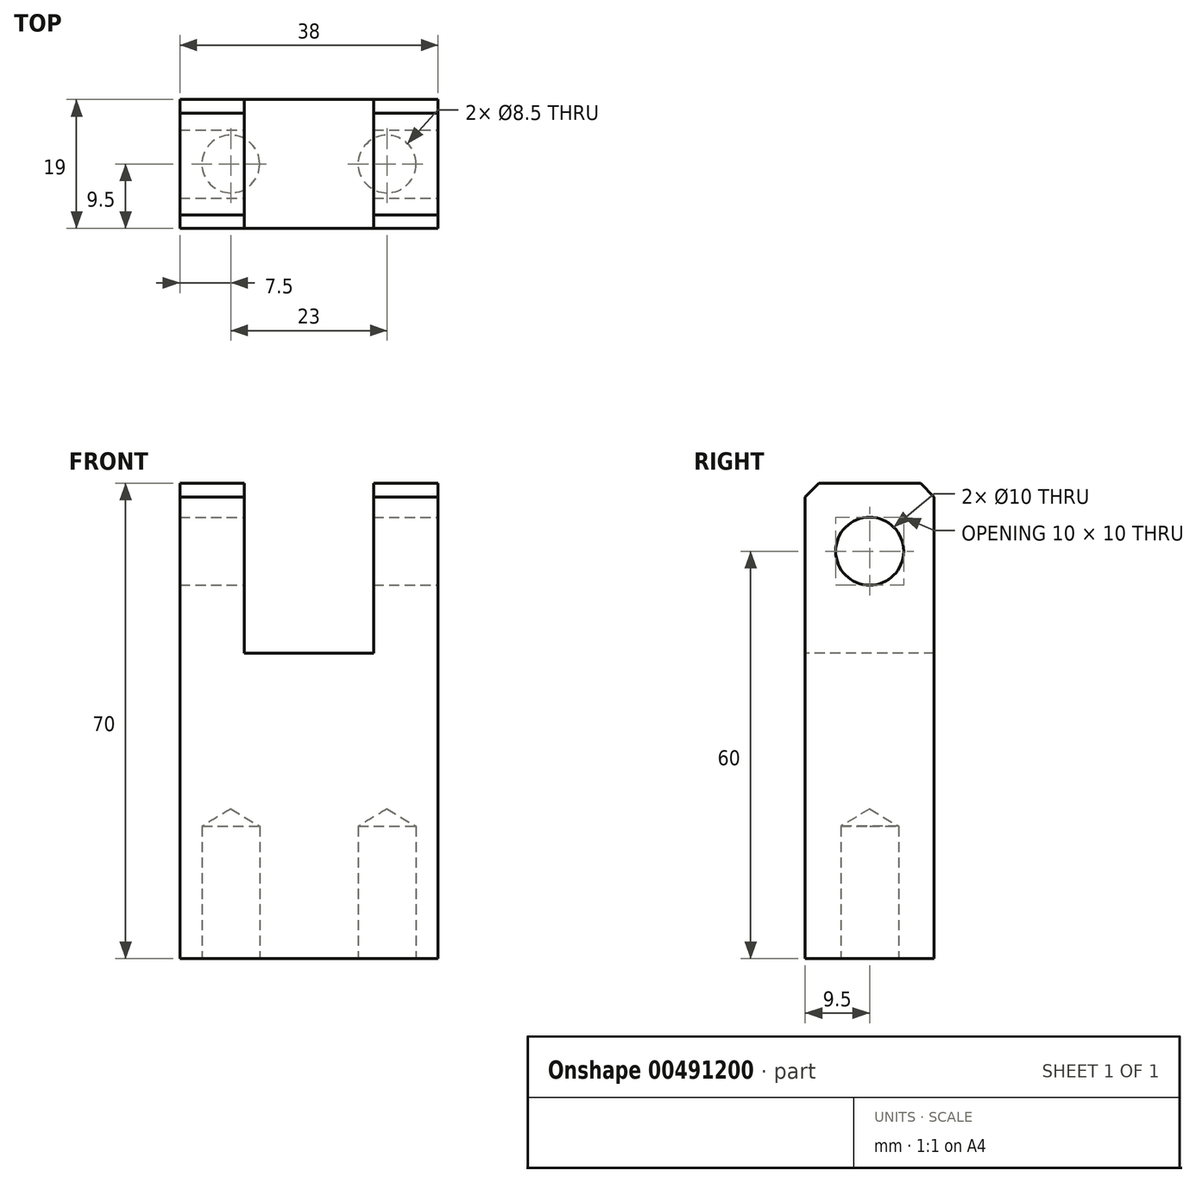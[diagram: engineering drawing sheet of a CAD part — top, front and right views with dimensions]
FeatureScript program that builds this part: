
annotation { "Feature Type Name" : "Feature", "Feature Type Description" : "" }
export const myFeature = defineFeature(function(context is Context, id is Id, definition is map)
    precondition{}
    {
        {
            var Q0;
            Q0=qCreatedBy(makeId("Front.planeOp"),FACE);
            var sketch = newSketch(context, id + "F0", { "sketchPlane" : qUnion([Q0])});
            skLineSegment(sketch, "E0.bottom", {"start": v(-19, 35) * mm, "end": v(19, 35) * mm});
            skLineSegment(sketch, "E0.top", {"start": v(-19, -35) * mm, "end": v(19, -35) * mm});
            skLineSegment(sketch, "E0.left", {"start": v(-19, 35) * mm, "end": v(-19, -35) * mm});
            skLineSegment(sketch, "E0.right", {"start": v(19, 35) * mm, "end": v(19, -35) * mm});
            skSolve(sketch);
        }
        {
            var Q0;
            Q0=makeQuery(id+"F0.imprint","IMPRINT",FACE,{"disambiguationData":[TD([[makeQuery(id+"F0.imprint","IMPRINT",EDGE,{"derivedFrom":sQuery(id+"F0.wireOp",EDGE,"E0.bottom")}),-1.0]])]});
            extrude(context, id + "F1", {"entities" : qUnion([Q0]), "endBound" : BoundingType.SYMMETRIC, "depth" : 19 * mm});
        }
        {
            var Q0;
            Q0=makeQuery(id+"F1.opExtrude","CAP_FACE",FACE,{"disambiguationData":[OSD([sQuery(id+"F0.wireOp",EDGE,"E0.bottom"),sQuery(id+"F0.wireOp",EDGE,"E0.top"),sQuery(id+"F0.wireOp",EDGE,"E0.left"),sQuery(id+"F0.wireOp",EDGE,"E0.right")])],"isStart":false});
            var sketch = newSketch(context, id + "F2", { "sketchPlane" : qUnion([Q0])});
            skLineSegment(sketch, "E1.bottom", {"start": v(-9.5, 35) * mm, "end": v(9.5, 35) * mm});
            skLineSegment(sketch, "E1.top", {"start": v(-9.5, 10) * mm, "end": v(9.5, 10) * mm});
            skLineSegment(sketch, "E1.left", {"start": v(-9.5, 35) * mm, "end": v(-9.5, 10) * mm});
            skLineSegment(sketch, "E1.right", {"start": v(9.5, 35) * mm, "end": v(9.5, 10) * mm});
            skSolve(sketch);
        }
        {
            var Q0;
            Q0=makeQuery(id+"F2.imprint","IMPRINT",FACE,{"disambiguationData":[TD([[makeQuery(id+"F2.imprint","IMPRINT",EDGE,{"derivedFrom":sQuery(id+"F2.wireOp",EDGE,"E1.bottom")}),-1.0]])]});
            extrude(context, id + "F3", {"entities" : qUnion([Q0]), "operationType" : NewBodyOperationType.REMOVE, "oppositeDirection" : true, "depth" : 19 * mm});
        }
        {
            var Q0;
            Q0=makeQuery(id+"F1.opExtrude","SWEPT_FACE",FACE,{"disambiguationData":[OSD([sQuery(id+"F0.wireOp",EDGE,"E0.right")])]});
            var sketch = newSketch(context, id + "F4", { "sketchPlane" : qUnion([Q0])});
            skCircle(sketch, "E2", {"center": v(0, 25) * mm, "radius": 5 * mm});
            skSolve(sketch);
        }
        {
            var Q0;
            Q0=makeQuery(id+"F4.imprint","IMPRINT",FACE,{"disambiguationData":[TD([[makeQuery(id+"F4.imprint","IMPRINT",EDGE,{"derivedFrom":sQuery(id+"F4.wireOp",EDGE,"E2")}),1.0]])]});
            extrude(context, id + "F5", {"entities" : qUnion([Q0]), "operationType" : NewBodyOperationType.REMOVE, "oppositeDirection" : true, "depth" : 38 * mm});
        }
        {
            var Q0;
            {var subQ0=sQuery(id+"F0.wireOp",EDGE,"E0.bottom");var subQ1=sQuery(id+"F0.wireOp",EDGE,"E0.right");Q0=makeQuery(id+"F3.boolean.opBoolean","SPLIT",EDGE,{"disambiguationData":[TD([makeQuery(id+"F1.opExtrude","SWEPT_FACE",FACE,{"disambiguationData":[OSD([subQ1])]})])],"derivedFrom":makeQuery(id+"F1.opExtrude","CAP_EDGE",EDGE,{"disambiguationData":[OSD([subQ0])],"isStart":true})});}
            var Q1;
            {var subQ0=sQuery(id+"F0.wireOp",EDGE,"E0.bottom");var subQ1=sQuery(id+"F0.wireOp",EDGE,"E0.left");Q1=makeQuery(id+"F3.boolean.opBoolean","SPLIT",EDGE,{"disambiguationData":[TD([makeQuery(id+"F1.opExtrude","SWEPT_FACE",FACE,{"disambiguationData":[OSD([subQ1])]})])],"derivedFrom":makeQuery(id+"F1.opExtrude","CAP_EDGE",EDGE,{"disambiguationData":[OSD([subQ0])],"isStart":true})});}
            var Q2;
            {var subQ0=sQuery(id+"F0.wireOp",EDGE,"E0.bottom");var subQ1=sQuery(id+"F0.wireOp",EDGE,"E0.left");Q2=makeQuery(id+"F3.boolean.opBoolean","SPLIT",EDGE,{"disambiguationData":[TD([makeQuery(id+"F1.opExtrude","SWEPT_FACE",FACE,{"disambiguationData":[OSD([subQ1])]})])],"derivedFrom":makeQuery(id+"F1.opExtrude","CAP_EDGE",EDGE,{"disambiguationData":[OSD([subQ0])],"isStart":false})});}
            var Q3;
            {var subQ0=sQuery(id+"F0.wireOp",EDGE,"E0.bottom");var subQ1=sQuery(id+"F0.wireOp",EDGE,"E0.right");Q3=makeQuery(id+"F3.boolean.opBoolean","SPLIT",EDGE,{"disambiguationData":[TD([makeQuery(id+"F1.opExtrude","SWEPT_FACE",FACE,{"disambiguationData":[OSD([subQ1])]})])],"derivedFrom":makeQuery(id+"F1.opExtrude","CAP_EDGE",EDGE,{"disambiguationData":[OSD([subQ0])],"isStart":false})});}
            chamfer(context, id + "F6", {"entities" : qUnion([Q0, Q1, Q2, Q3]), "width" : 2 * mm, "tangentPropagation" : true});
        }
        {
            var Q0;
            Q0=makeQuery(id+"F1.opExtrude","SWEPT_FACE",FACE,{"disambiguationData":[OSD([sQuery(id+"F0.wireOp",EDGE,"E0.top")])]});
            var sketch = newSketch(context, id + "F7", { "sketchPlane" : qUnion([Q0])});
            skPoint(sketch, "E3", {"position": v(-11.5, 0) * mm});
            skPoint(sketch, "E4", {"position": v(11.5, 0) * mm});
            skSolve(sketch);
        }
        {
            var Q0;
            Q0=sQuery(id+"F7.wireOp",VERTEX,"E3");
            var Q1;
            Q1=sQuery(id+"F7.wireOp",VERTEX,"E4");
            var Q2;
            Q2=makeQuery(id+"F1.opExtrude","SWEPT_BODY",BODY,{"disambiguationData":[OSD([sQuery(id+"F0.wireOp",EDGE,"E0.bottom"),sQuery(id+"F0.wireOp",EDGE,"E0.top"),sQuery(id+"F0.wireOp",EDGE,"E0.left"),sQuery(id+"F0.wireOp",EDGE,"E0.right")])]});
            hole(context, id + "F8", {"style" : HoleStyle.SIMPLE, "endStyle" : HoleEndStyle.BLIND, "standardTappedOrClearance" : lookupTablePath({ "standard" : "ISO", "engagement" : "75%", "pitch" : "1.5 mm", "size" : "M10", "type" : "Tapped" }), "standardBlindInLast" : lookupTablePath({ "standard" : "ISO", "engagement" : "75%", "pitch" : "1.5 mm", "size" : "M10", "type" : "Tapped" }), "holeDiameter" : 8.5 * mm, "showTappedDepth" : true, "holeDepth" : 19.5 * mm, "isTappedThrough" : true, "tappedDepth" : 15 * mm, "tapClearance" : 3, "locations" : qUnion([Q0, Q1]), "scope" : qUnion([Q2]), "majorDiameter" : 10 * mm});
        }
    });
